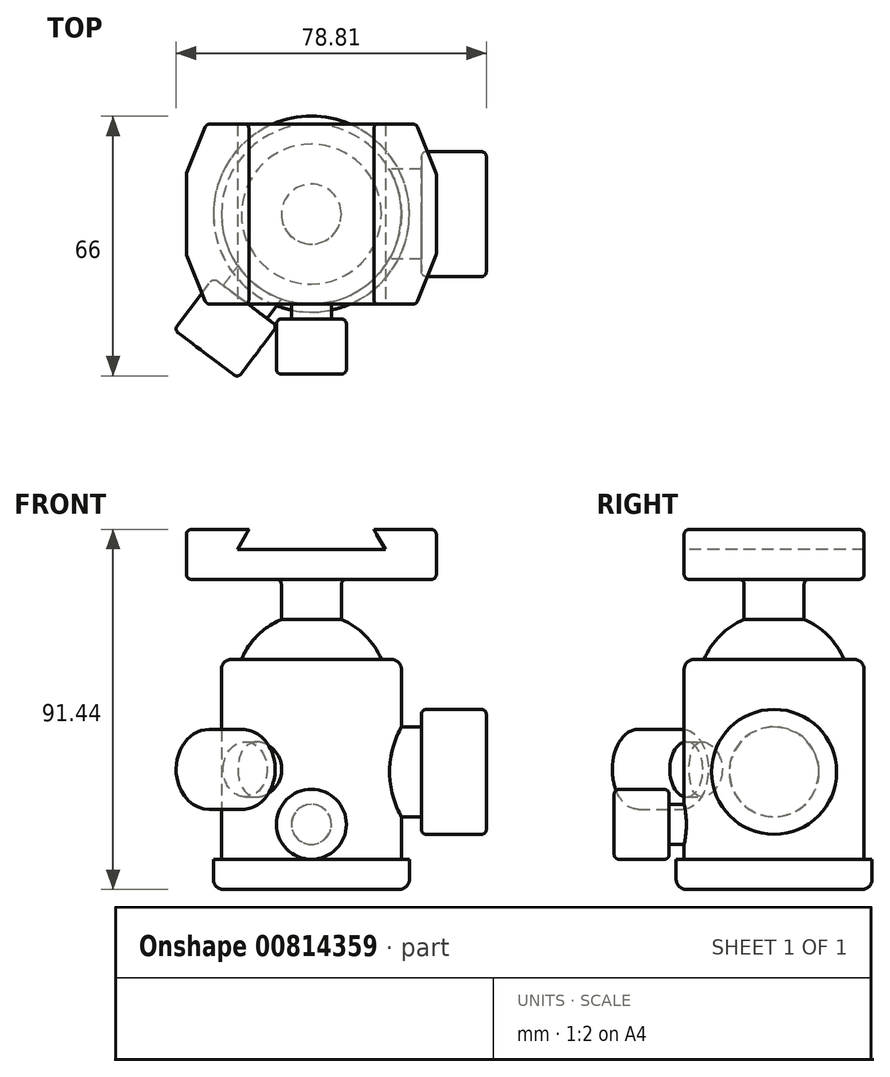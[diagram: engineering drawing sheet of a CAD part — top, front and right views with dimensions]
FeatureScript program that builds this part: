
annotation { "Feature Type Name" : "Feature", "Feature Type Description" : "" }
export const myFeature = defineFeature(function(context is Context, id is Id, definition is map)
    precondition{}
    {
        {
            var Q0;
            Q0=qCreatedBy(makeId("Right.planeOp"),FACE);
            var sketch = newSketch(context, id + "F0", { "sketchPlane" : qUnion([Q0])});
            skLineSegment(sketch, "E0", {"start": v(0, -49.38) * mm, "end": v(0, 104.09) * mm, "construction": true});
            skLineSegment(sketch, "E1", {"start": v(0, 0) * mm, "end": v(-24.9, 0) * mm});
            skLineSegment(sketch, "E2", {"start": v(-24.9, 0) * mm, "end": v(-24.9, 7.62) * mm});
            skLineSegment(sketch, "E3", {"start": v(-24.9, 7.62) * mm, "end": v(-22.86, 7.62) * mm});
            skLineSegment(sketch, "E4", {"start": v(-22.86, 7.62) * mm, "end": v(-22.86, 58.42) * mm});
            skLineSegment(sketch, "E5", {"start": v(-22.86, 58.42) * mm, "end": v(-17.78, 58.42) * mm});
            skArc(sketch, "E6", {"start": v(-7.62, 68.58) * mm, "mid": v(-13.68, 64.48) * mm, "end": v(-17.78, 58.42) * mm});
            skLineSegment(sketch, "E7", {"start": v(-7.62, 68.58) * mm, "end": v(-7.62, 78.74) * mm});
            skLineSegment(sketch, "E8", {"start": v(-7.62, 78.74) * mm, "end": v(0, 78.74) * mm});
            skLineSegment(sketch, "E9", {"start": v(0, 78.74) * mm, "end": v(0, 0) * mm});
            skSolve(sketch);
        }
        {
            var Q0;
            Q0 = qSketchRegion(id + "F0", true);
            var Q1;
            Q1=sQuery(id+"F0.wireOp",EDGE,"E0");
            revolve(context, id + "F1", {"surfaceOperationType" : NewSurfaceOperationType.NEW, "entities" : qUnion([Q0]), "axis" : qUnion([Q1]), "revolveType" : RevolveType.FULL});
        }
        {
            var Q0;
            Q0=makeQuery(id+"F1.opRevolve","SWEPT_FACE",FACE,{"disambiguationData":[OSD([sQuery(id+"F0.wireOp",EDGE,"E8")])]});
            var sketch = newSketch(context, id + "F2", { "sketchPlane" : qUnion([Q0])});
            skLineSegment(sketch, "E10.bottom", {"start": v(-31.75, 22.86) * mm, "end": v(31.75, 22.86) * mm});
            skLineSegment(sketch, "E10.top", {"start": v(-31.75, -22.86) * mm, "end": v(31.75, -22.86) * mm});
            skLineSegment(sketch, "E10.left", {"start": v(-31.75, 22.86) * mm, "end": v(-31.75, -22.86) * mm});
            skLineSegment(sketch, "E10.right", {"start": v(31.75, 22.86) * mm, "end": v(31.75, -22.86) * mm});
            skPoint(sketch, "E10.middle", {"position": v(0, 0) * mm});
            skSolve(sketch);
        }
        {
            var Q0;
            Q0 = qSketchRegion(id + "F2", true);
            extrude(context, id + "F3", {"entities" : qUnion([Q0]), "operationType" : NewBodyOperationType.ADD, "depth" : 12.7 * mm, "offsetDistance" : 25.4 * mm});
        }
        {
            var Q0;
            Q0=makeQuery(id+"F3.opExtrude","SWEPT_FACE",FACE,{"disambiguationData":[OSD([sQuery(id+"F2.wireOp",EDGE,"E10.top")])]});
            var sketch = newSketch(context, id + "F4", { "sketchPlane" : qUnion([Q0])});
            skLineSegment(sketch, "E11.0.0", {"start": v(-31.75, 78.74) * mm, "end": v(31.75, 78.74) * mm, "construction": true});
            skLineSegment(sketch, "E11.0.1", {"start": v(31.75, 78.74) * mm, "end": v(31.75, 91.44) * mm, "construction": true});
            skLineSegment(sketch, "E11.0.2", {"start": v(31.75, 91.44) * mm, "end": v(-31.75, 91.44) * mm, "construction": true});
            skLineSegment(sketch, "E11.0.3", {"start": v(-31.75, 91.44) * mm, "end": v(-31.75, 78.74) * mm, "construction": true});
            skLineSegment(sketch, "E12", {"start": v(-18.8, 86.36) * mm, "end": v(18.8, 86.36) * mm});
            skLineSegment(sketch, "E13", {"start": v(18.8, 86.36) * mm, "end": v(15.87, 91.44) * mm});
            skLineSegment(sketch, "E14", {"start": v(15.87, 91.44) * mm, "end": v(-15.88, 91.44) * mm});
            skLineSegment(sketch, "E15", {"start": v(-15.88, 91.44) * mm, "end": v(-18.8, 86.36) * mm});
            skLineSegment(sketch, "E16", {"start": v(0, 78.74) * mm, "end": v(0, 91.44) * mm, "construction": true});
            skSolve(sketch);
        }
        {
            var Q0;
            Q0 = qSketchRegion(id + "F4", true);
            extrude(context, id + "F5", {"entities" : qUnion([Q0]), "operationType" : NewBodyOperationType.REMOVE, "endBound" : BoundingType.THROUGH_ALL, "oppositeDirection" : true, "depth" : 25.4 * mm, "offsetDistance" : 25.4 * mm});
        }
        {
            var Q0;
            Q0=qCreatedBy(makeId("Right.planeOp"),FACE);
            var sketch = newSketch(context, id + "F6", { "sketchPlane" : qUnion([Q0])});
            skLineSegment(sketch, "E17", {"start": v(0, 16.51) * mm, "end": v(-33.66, 16.51) * mm, "construction": true});
            skLineSegment(sketch, "E18.bottom", {"start": v(0, 21.6) * mm, "end": v(-26.67, 21.6) * mm});
            skLineSegment(sketch, "E18.top", {"start": v(0, 11.43) * mm, "end": v(-26.67, 11.43) * mm});
            skLineSegment(sketch, "E18.left", {"start": v(0, 21.6) * mm, "end": v(0, 11.43) * mm});
            skLineSegment(sketch, "E18.right", {"start": v(-26.67, 21.6) * mm, "end": v(-26.67, 11.43) * mm});
            skPoint(sketch, "E18.middle", {"position": v(-13.34, 16.51) * mm});
            skLineSegment(sketch, "E19.bottom", {"start": v(-26.67, 25.4) * mm, "end": v(-40.64, 25.4) * mm});
            skLineSegment(sketch, "E19.top", {"start": v(-26.67, 7.62) * mm, "end": v(-40.64, 7.62) * mm});
            skLineSegment(sketch, "E19.left", {"start": v(-26.67, 25.4) * mm, "end": v(-26.67, 7.62) * mm});
            skLineSegment(sketch, "E19.right", {"start": v(-40.64, 25.4) * mm, "end": v(-40.64, 7.62) * mm});
            skPoint(sketch, "E19.middle", {"position": v(-33.66, 16.51) * mm});
            skLineSegment(sketch, "E20", {"start": v(22.86, 7.62) * mm, "end": v(22.86, 58.42) * mm, "construction": true});
            skLineSegment(sketch, "E21", {"start": v(-22.86, 58.42) * mm, "end": v(-22.86, 7.62) * mm, "construction": true});
            skLineSegment(sketch, "E22", {"start": v(0, 16.51) * mm, "end": v(-40.64, 16.51) * mm});
            skSolve(sketch);
        }
        {
            var Q0;
            {var subQ1=sQuery(id+"F6.wireOp",EDGE,"E19.bottom");Q0=makeQuery(id+"F6.imprint","IMPRINT",FACE,{"disambiguationData":[TD([[makeQuery(id+"F6.imprint","IMPRINT",EDGE,{"derivedFrom":subQ1}),1.0]])]});}
            var Q1;
            {var subQ0=sQuery(id+"F6.wireOp",EDGE,"E18.bottom");Q1=makeQuery(id+"F6.imprint","IMPRINT",FACE,{"disambiguationData":[TD([[makeQuery(id+"F6.imprint","IMPRINT",EDGE,{"derivedFrom":subQ0}),1.0]])]});}
            var Q2;
            Q2=sQuery(id+"F6.wireOp",EDGE,"E22");
            revolve(context, id + "F7", {"operationType" : NewBodyOperationType.ADD, "surfaceOperationType" : NewSurfaceOperationType.NEW, "entities" : qUnion([Q0, Q1]), "axis" : qUnion([Q2]), "revolveType" : RevolveType.FULL});
        }
        {
            var Q0;
            Q0=qCreatedBy(makeId("Front.planeOp"),FACE);
            var sketch = newSketch(context, id + "F8", { "sketchPlane" : qUnion([Q0])});
            skLineSegment(sketch, "E23", {"start": v(0, 29.85) * mm, "end": v(60.7, 29.85) * mm, "construction": true});
            skLineSegment(sketch, "E24.bottom", {"start": v(0, 41.27) * mm, "end": v(27.94, 41.27) * mm});
            skLineSegment(sketch, "E24.top", {"start": v(0, 18.41) * mm, "end": v(27.94, 18.41) * mm});
            skLineSegment(sketch, "E24.left", {"start": v(0, 41.27) * mm, "end": v(0, 18.41) * mm});
            skLineSegment(sketch, "E24.right", {"start": v(27.94, 41.27) * mm, "end": v(27.94, 18.41) * mm});
            skPoint(sketch, "E24.middle", {"position": v(13.97, 29.85) * mm});
            skLineSegment(sketch, "E25.bottom", {"start": v(27.94, 45.72) * mm, "end": v(44.45, 45.72) * mm});
            skLineSegment(sketch, "E25.top", {"start": v(27.94, 13.97) * mm, "end": v(44.45, 13.97) * mm});
            skLineSegment(sketch, "E25.left", {"start": v(27.94, 45.72) * mm, "end": v(27.94, 13.97) * mm});
            skLineSegment(sketch, "E25.right", {"start": v(44.45, 45.72) * mm, "end": v(44.45, 13.97) * mm});
            skPoint(sketch, "E25.middle", {"position": v(36.2, 29.85) * mm});
            skLineSegment(sketch, "E26", {"start": v(0, 29.85) * mm, "end": v(44.45, 29.85) * mm});
            skLineSegment(sketch, "E27", {"start": v(22.86, 7.62) * mm, "end": v(22.86, 58.42) * mm, "construction": true});
            skLineSegment(sketch, "E28", {"start": v(-22.86, 58.42) * mm, "end": v(-22.86, 7.62) * mm, "construction": true});
            skSolve(sketch);
        }
        {
            var Q0;
            {var subQ1=sQuery(id+"F8.wireOp",EDGE,"E25.bottom");Q0=makeQuery(id+"F8.imprint","IMPRINT",FACE,{"disambiguationData":[TD([[makeQuery(id+"F8.imprint","IMPRINT",EDGE,{"derivedFrom":subQ1}),-1.0]])]});}
            var Q1;
            {var subQ0=sQuery(id+"F8.wireOp",EDGE,"E24.bottom");Q1=makeQuery(id+"F8.imprint","IMPRINT",FACE,{"disambiguationData":[TD([[makeQuery(id+"F8.imprint","IMPRINT",EDGE,{"derivedFrom":subQ0}),-1.0]])]});}
            var Q2;
            Q2=sQuery(id+"F8.wireOp",EDGE,"E23");
            revolve(context, id + "F9", {"operationType" : NewBodyOperationType.ADD, "surfaceOperationType" : NewSurfaceOperationType.NEW, "entities" : qUnion([Q0, Q1]), "axis" : qUnion([Q2]), "revolveType" : RevolveType.FULL});
        }
        {
            var Q0;
            Q0=sQuery(id+"F0.wireOp",EDGE,"E0");
            var Q1;
            Q1=qCreatedBy(makeId("Right.planeOp"),FACE);
            cPlane(context, id + "F10", {"entities" : qUnion([Q0, Q1]), "cplaneType" : CPlaneType.LINE_ANGLE, "offset" : 25.4 * mm, "angle" : 37 * degree, "oppositeDirection" : true, "width" : 152.4 * mm, "height" : 152.4 * mm});
        }
        {
            var Q0;
            Q0=qCreatedBy(id+"F10.planeOp",FACE);
            var sketch = newSketch(context, id + "F11", { "sketchPlane" : qUnion([Q0])});
            skLineSegment(sketch, "E29", {"start": v(0, 30.48) * mm, "end": v(40.7, 30.48) * mm, "construction": true});
            skLineSegment(sketch, "E30.bottom", {"start": v(0, 37.47) * mm, "end": v(27.94, 37.47) * mm});
            skLineSegment(sketch, "E30.top", {"start": v(0, 23.5) * mm, "end": v(27.94, 23.5) * mm});
            skLineSegment(sketch, "E30.left", {"start": v(0, 37.47) * mm, "end": v(0, 23.5) * mm});
            skLineSegment(sketch, "E30.right", {"start": v(27.94, 37.47) * mm, "end": v(27.94, 23.5) * mm});
            skPoint(sketch, "E30.middle", {"position": v(13.97, 30.48) * mm});
            skLineSegment(sketch, "E31.bottom", {"start": v(27.94, 40.64) * mm, "end": v(44.45, 40.64) * mm});
            skLineSegment(sketch, "E31.top", {"start": v(27.94, 20.32) * mm, "end": v(44.45, 20.32) * mm});
            skLineSegment(sketch, "E31.left", {"start": v(27.94, 40.64) * mm, "end": v(27.94, 20.32) * mm});
            skLineSegment(sketch, "E31.right", {"start": v(44.45, 40.64) * mm, "end": v(44.45, 20.32) * mm});
            skPoint(sketch, "E31.middle", {"position": v(36.2, 30.48) * mm});
            skLineSegment(sketch, "E32", {"start": v(22.86, 7.62) * mm, "end": v(22.86, 58.42) * mm, "construction": true});
            skLineSegment(sketch, "E33", {"start": v(-22.86, 58.42) * mm, "end": v(-22.86, 7.62) * mm, "construction": true});
            skLineSegment(sketch, "E34", {"start": v(0, 30.48) * mm, "end": v(44.45, 30.48) * mm});
            skSolve(sketch);
        }
        {
            var Q0;
            {var subQ0=sQuery(id+"F11.wireOp",EDGE,"E30.bottom");Q0=makeQuery(id+"F11.imprint","IMPRINT",FACE,{"disambiguationData":[TD([[makeQuery(id+"F11.imprint","IMPRINT",EDGE,{"derivedFrom":subQ0}),-1.0]])]});}
            var Q1;
            {var subQ1=sQuery(id+"F11.wireOp",EDGE,"E31.bottom");Q1=makeQuery(id+"F11.imprint","IMPRINT",FACE,{"disambiguationData":[TD([[makeQuery(id+"F11.imprint","IMPRINT",EDGE,{"derivedFrom":subQ1}),-1.0]])]});}
            var Q2;
            Q2=sQuery(id+"F11.wireOp",EDGE,"E34");
            revolve(context, id + "F12", {"operationType" : NewBodyOperationType.ADD, "surfaceOperationType" : NewSurfaceOperationType.NEW, "entities" : qUnion([Q0, Q1]), "axis" : qUnion([Q2]), "revolveType" : RevolveType.FULL});
        }
        {
            var Q0;
            Q0=makeQuery(id+"F1.opRevolve","SWEPT_EDGE",EDGE,{"disambiguationData":[OSD([sQuery(id+"F0.wireOp",EDGE,"E1"),sQuery(id+"F0.wireOp",EDGE,"E2")])]});
            var Q1;
            Q1=makeQuery(id+"F1.opRevolve","SWEPT_EDGE",EDGE,{"disambiguationData":[OSD([sQuery(id+"F0.wireOp",EDGE,"E4"),sQuery(id+"F0.wireOp",EDGE,"E5")])]});
            fillet(context, id + "F13", {"entities" : qUnion([Q0, Q1]), "radius" : 2.54 * mm, "tangentPropagation" : true, "allowEdgeOverflow" : false});
        }
        {
            var Q0;
            Q0=makeQuery(id+"F12.opRevolve","SWEPT_FACE",FACE,{"disambiguationData":[OSD([sQuery(id+"F11.wireOp",EDGE,"E31.right")])]});
            var Q1;
            Q1=makeQuery(id+"F7.opRevolve","SWEPT_FACE",FACE,{"disambiguationData":[OSD([sQuery(id+"F6.wireOp",EDGE,"E19.right")])]});
            var Q2;
            Q2=makeQuery(id+"F9.opRevolve","SWEPT_FACE",FACE,{"disambiguationData":[OSD([sQuery(id+"F8.wireOp",EDGE,"E25.right")])]});
            var Q3;
            Q3=makeQuery(id+"F9.opRevolve","SWEPT_EDGE",EDGE,{"disambiguationData":[OSD([sQuery(id+"F8.wireOp",EDGE,"E25.bottom"),sQuery(id+"F8.wireOp",EDGE,"E25.left")])]});
            var Q4;
            Q4=makeQuery(id+"F7.opRevolve","SWEPT_EDGE",EDGE,{"disambiguationData":[OSD([sQuery(id+"F6.wireOp",EDGE,"E19.bottom"),sQuery(id+"F6.wireOp",EDGE,"E19.left")])]});
            var Q5;
            Q5=makeQuery(id+"F12.opRevolve","SWEPT_EDGE",EDGE,{"disambiguationData":[OSD([sQuery(id+"F11.wireOp",EDGE,"E31.bottom"),sQuery(id+"F11.wireOp",EDGE,"E31.left")])]});
            fillet(context, id + "F14", {"entities" : qUnion([Q0, Q1, Q2, Q3, Q4, Q5]), "radius" : 1.27 * mm, "tangentPropagation" : true, "allowEdgeOverflow" : false});
        }
        {
            var Q0;
            Q0=makeQuery(id+"F3.opExtrude","SWEPT_EDGE",EDGE,{"disambiguationData":[OSD([sQuery(id+"F2.wireOp",EDGE,"E10.bottom"),sQuery(id+"F2.wireOp",EDGE,"E10.left")])]});
            var Q1;
            Q1=makeQuery(id+"F3.opExtrude","SWEPT_EDGE",EDGE,{"disambiguationData":[OSD([sQuery(id+"F2.wireOp",EDGE,"E10.top"),sQuery(id+"F2.wireOp",EDGE,"E10.left")])]});
            var Q2;
            Q2=makeQuery(id+"F3.opExtrude","SWEPT_EDGE",EDGE,{"disambiguationData":[OSD([sQuery(id+"F2.wireOp",EDGE,"E10.top"),sQuery(id+"F2.wireOp",EDGE,"E10.right")])]});
            var Q3;
            Q3=makeQuery(id+"F3.opExtrude","SWEPT_EDGE",EDGE,{"disambiguationData":[OSD([sQuery(id+"F2.wireOp",EDGE,"E10.bottom"),sQuery(id+"F2.wireOp",EDGE,"E10.right")])]});
            chamfer(context, id + "F15", {"entities" : qUnion([Q0, Q1, Q2, Q3]), "chamferType" : ChamferType.TWO_OFFSETS, "width1" : 12.7 * mm, "oppositeDirection" : false, "width2" : 5.08 * mm, "tangentPropagation" : true});
        }
        {
            var Q0;
            Q0=makeQuery(id+"F3.opExtrude","SWEPT_FACE",FACE,{"disambiguationData":[OSD([sQuery(id+"F2.wireOp",EDGE,"E10.left")])]});
            var Q1;
            Q1=makeQuery(id+"F15.opChamfer","BLEND_FACE",FACE,{"disambiguationData":[OSD([sQuery(id+"F2.wireOp",EDGE,"E10.top"),sQuery(id+"F2.wireOp",EDGE,"E10.left")])]});
            var Q2;
            Q2=makeQuery(id+"F15.opChamfer","BLEND_FACE",FACE,{"disambiguationData":[OSD([sQuery(id+"F2.wireOp",EDGE,"E10.bottom"),sQuery(id+"F2.wireOp",EDGE,"E10.left")])]});
            var Q3;
            Q3=makeQuery(id+"F15.opChamfer","BLEND_FACE",FACE,{"disambiguationData":[OSD([sQuery(id+"F2.wireOp",EDGE,"E10.bottom"),sQuery(id+"F2.wireOp",EDGE,"E10.right")])]});
            var Q4;
            Q4=makeQuery(id+"F3.opExtrude","SWEPT_FACE",FACE,{"disambiguationData":[OSD([sQuery(id+"F2.wireOp",EDGE,"E10.right")])]});
            var Q5;
            Q5=makeQuery(id+"F15.opChamfer","BLEND_FACE",FACE,{"disambiguationData":[OSD([sQuery(id+"F2.wireOp",EDGE,"E10.top"),sQuery(id+"F2.wireOp",EDGE,"E10.right")])]});
            var Q6;
            {var subQ0=sQuery(id+"F2.wireOp",EDGE,"E10.left");var subQ1=sQuery(id+"F2.wireOp",EDGE,"E10.top");Q6=makeQuery(id+"F5.boolean.opBoolean","SPLIT",EDGE,{"disambiguationData":[TD([makeQuery(id+"F3.opExtrude","SWEPT_FACE",FACE,{"disambiguationData":[OSD([subQ0])]})])],"derivedFrom":makeQuery(id+"F3.opExtrude","CAP_EDGE",EDGE,{"disambiguationData":[OSD([subQ1])],"isStart":false})});}
            var Q7;
            {var subQ0=sQuery(id+"F2.wireOp",EDGE,"E10.right");var subQ1=sQuery(id+"F2.wireOp",EDGE,"E10.top");Q7=makeQuery(id+"F5.boolean.opBoolean","SPLIT",EDGE,{"disambiguationData":[TD([makeQuery(id+"F3.opExtrude","SWEPT_FACE",FACE,{"disambiguationData":[OSD([subQ0])]})])],"derivedFrom":makeQuery(id+"F3.opExtrude","CAP_EDGE",EDGE,{"disambiguationData":[OSD([subQ1])],"isStart":false})});}
            var Q8;
            {var subQ0=sQuery(id+"F2.wireOp",EDGE,"E10.bottom");var subQ1=sQuery(id+"F2.wireOp",EDGE,"E10.right");Q8=makeQuery(id+"F5.boolean.opBoolean","SPLIT",EDGE,{"disambiguationData":[TD([makeQuery(id+"F3.opExtrude","SWEPT_FACE",FACE,{"disambiguationData":[OSD([subQ1])]})])],"derivedFrom":makeQuery(id+"F3.opExtrude","CAP_EDGE",EDGE,{"disambiguationData":[OSD([subQ0])],"isStart":false})});}
            var Q9;
            {var subQ0=sQuery(id+"F2.wireOp",EDGE,"E10.bottom");var subQ1=sQuery(id+"F2.wireOp",EDGE,"E10.left");Q9=makeQuery(id+"F5.boolean.opBoolean","SPLIT",EDGE,{"disambiguationData":[TD([makeQuery(id+"F3.opExtrude","SWEPT_FACE",FACE,{"disambiguationData":[OSD([subQ1])]})])],"derivedFrom":makeQuery(id+"F3.opExtrude","CAP_EDGE",EDGE,{"disambiguationData":[OSD([subQ0])],"isStart":false})});}
            var Q10;
            Q10=makeQuery(id+"F3.opExtrude","CAP_FACE",FACE,{"disambiguationData":[OSD([sQuery(id+"F2.wireOp",EDGE,"E10.bottom"),sQuery(id+"F2.wireOp",EDGE,"E10.top"),sQuery(id+"F2.wireOp",EDGE,"E10.left"),sQuery(id+"F2.wireOp",EDGE,"E10.right")])],"isStart":true});
            fillet(context, id + "F16", {"entities" : qUnion([Q0, Q1, Q2, Q3, Q4, Q5, Q6, Q7, Q8, Q9, Q10]), "radius" : 1.27 * mm, "tangentPropagation" : true, "allowEdgeOverflow" : false});
        }
    });
